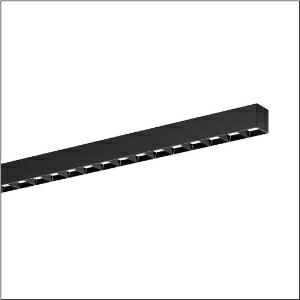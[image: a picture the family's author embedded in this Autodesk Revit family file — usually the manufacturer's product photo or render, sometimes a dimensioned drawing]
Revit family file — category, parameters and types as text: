
# Revit family: silica_21_51mx21dc4abb
name_source: partatom
category: Lighting Fixtures
units: mm (PartAtom-declared; Revit-internal decimal feet)

## family parameters
Cut with Voids When Loaded = No
Host = Face
Light Source = No
Part Type = Normal
Room Calculation Point = No
Round Connector Dimension = Use Diameter
Shared = No

## types (1)
- --- (1 x LED, 10800 lm, 64.8 W, 4000K)
    Apparent Load = 65 VA
    CIE Flux Codes = 87 99 100 100 100
    Color Rendering = 80
    Color Temperature = 4000K
    Default Elevation = 1800 mm
    Description = Silica 21, office luminaire, primary light control with darklight reflector, of PMMA, black, CAT 2 (L<= 3000cd/m²), light emission: direct distribution, primary light characteristic: symmetric, installation type: surface-mounted, LED, rated luminous flux: 10.800lm, luminous efficacy: 167lm/W, light colour: 840, colour temperature: 4000K, control gear: DALI 2, with terminal, 3+2-pole, max. 2.5mm², mains connection: 220..240V, AC, 50/60Hz, rated input power: 64.8W, luminaire housing, of aluminium, matt jet black (RAL 9005), length: 3.004mm, width: 53mm, height: 53mm, protection rating (complete): IP20, insulation class (complete): insulation class I (protective earthing), certification: CE, permissible operating ambient temperature: 0..+35°C, standard: EN 50419, packaging unit: 1 piece
    Height = 53 mm
    Lamp = 1 x LED
    Lamp Light Flux = 10800 lm
    Lamp Power = 64.8 W
    Lamp count = 1
    Length = 3004 mm
    Luminous efficacy = 167 lm/W
    Manufacturer = Siteco
    ModVariant = No
    Model = 51MX21DC4ABB
    Mounting Place = Ceiling
    Mounting Type = Surface mounted
    Number of Poles = 1
    OnlyDefault = Yes
    Power Factor = 1
    Product Name = Silica 21
    Product group = office luminaire | ceiling mounted
    ProductGroupID = 301
    Protection Class = Protection class I
    Protection Degree = IP 20
    RLX_Detail_Level = 1
    RLX_Emergency_Light_Flux = 0 lm
    RLX_Emergency_Type = 0
    RLX_Emergency_Type_DB = No
    RlxData = <blob elided: 63561 chars, md5=68191afe>
    Socket = socket
    Standby Power = 0 W
    System Light Flux = 10800 lm
    System Power = 65 W
    Type Comments = factory setting: luminous flux: 100 % | dim-lin: 254 | 367 mA
    Type Image = l_1335908.jpg
    URL = http://relux.com
    VarID = @adj_125429
    Voltage = 0 V
    Weight = 0.00 kg
    Width = 53 mm

## geometry (parser evidence)
native form markers: Blend x4, Sweep x12
no freeform markers — native parametric forms only
